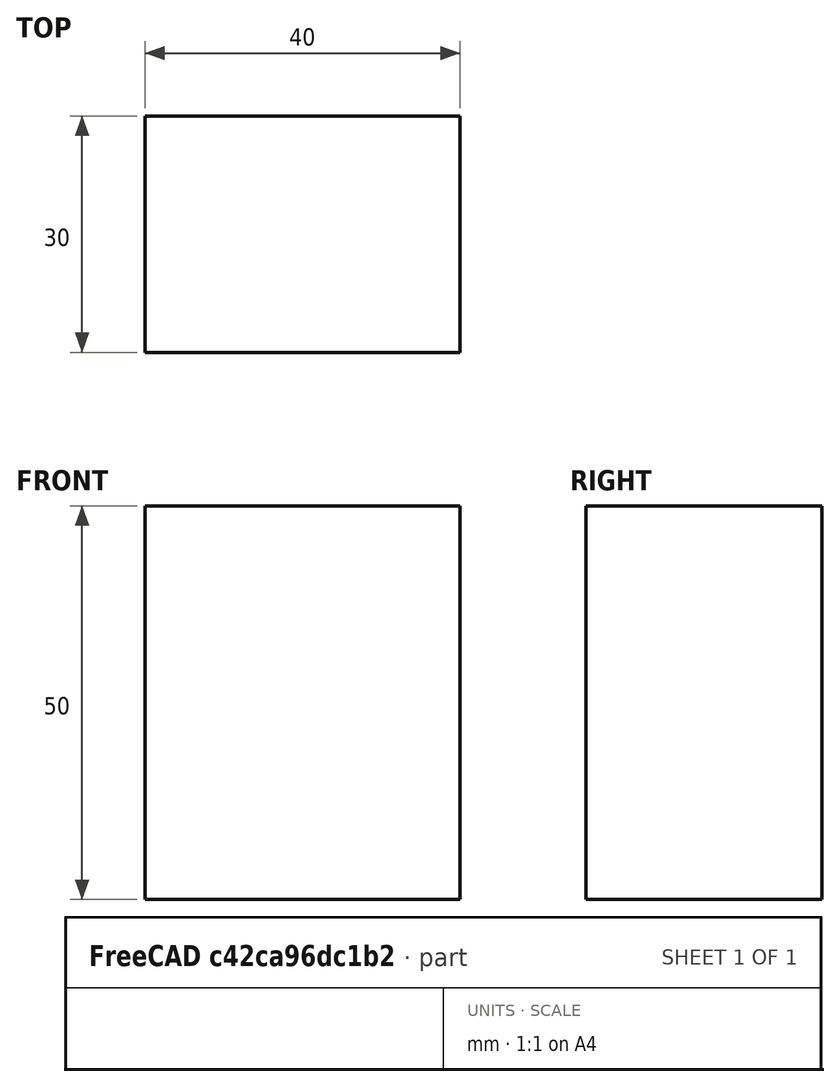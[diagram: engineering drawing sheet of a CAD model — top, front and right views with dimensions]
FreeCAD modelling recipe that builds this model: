
FCSTD DOCUMENT  (FreeCAD 0.15R4671 (Git))
Label: Flat Bar 40x30 EN10058 S235JR
License: All rights reserved
LicenseURL: http://en.wikipedia.org/wiki/All_rights_reserved
objects: Sketcher::SketchObject×1, Part::Extrusion×1
note: 2 computed .brp shape members not serialized (recipe doc carries the construction recipe); baked Part::Feature solids carry a one-line shape summary decoded from their .brp

FEATURE [Sketcher::SketchObject] Sketch
  sketch-geometry (4):
    g0: LineSegment StartX=-20 StartY=-15 StartZ=0 EndX=20 EndY=-15 EndZ=0
    g1: LineSegment StartX=20 StartY=-15 StartZ=0 EndX=20 EndY=15 EndZ=0
    g2: LineSegment StartX=20 StartY=15 StartZ=0 EndX=-20 EndY=15 EndZ=0
    g3: LineSegment StartX=-20 StartY=15 StartZ=0 EndX=-20 EndY=-15 EndZ=0
  constraints (12):
    c: Coincident(g0,g1)
    c: Coincident(g1,g2)
    c: Coincident(g2,g3)
    c: Coincident(g3,g0)
    c: Horizontal(g0)
    c: Horizontal(g2)
    c: Vertical(g1)
    c: Vertical(g3)
    c: Symmetric(g1,g2,g-2)
    c: Symmetric(g0,g1,g-1)
    c: DistanceY(g1) = 30
    c: DistanceX(g0) = 40
FEATURE [Part::Extrusion] Extrude  label="Flat Bar 40x30 EN10058 S235JR"
  Base = -> Sketch
  Dir = (0,0,50)
  Solid = true
